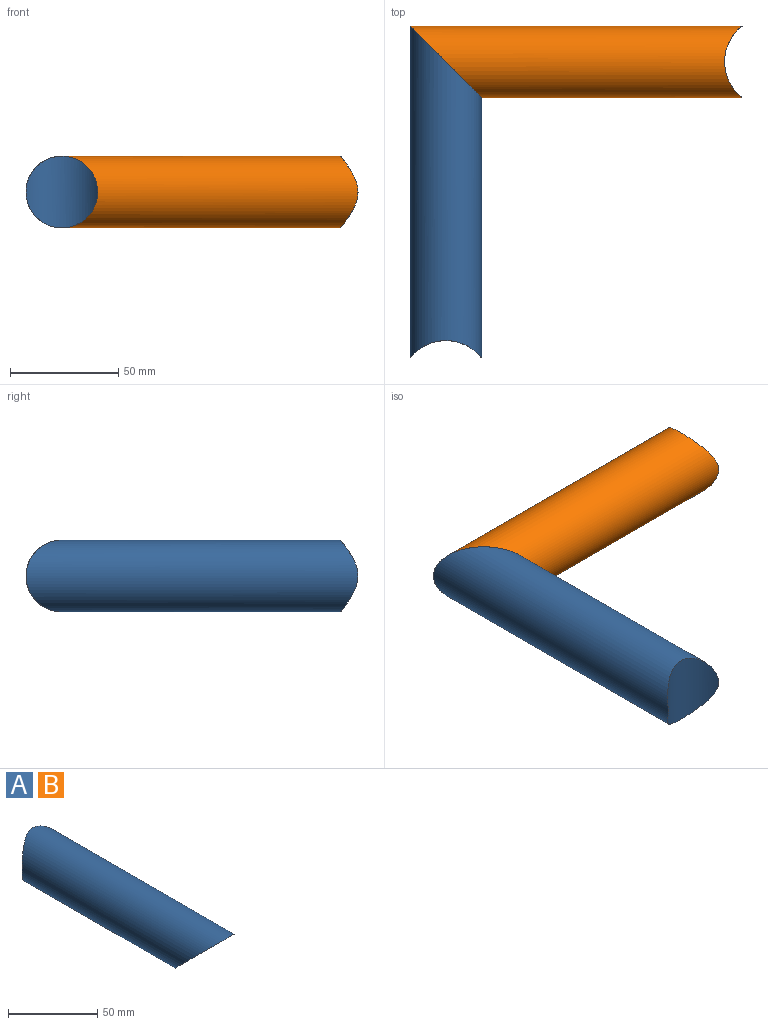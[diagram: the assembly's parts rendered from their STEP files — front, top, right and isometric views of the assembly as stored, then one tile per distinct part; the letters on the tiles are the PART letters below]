
ASSEMBLY  parts=2 mates=1
PART A: 3 faces, bbox 33x153x33 mm
  f0: cylinder r=16.5mm len=153.02mm, axis (0,1,0), area 13712.3mm2, adj f1,f2
  f1: plane 33x33mm, normal (0,-0.71,-0.71), area 1209.6mm2, adj f0
  f2: cylinder r=21mm len=33mm, axis (-1,0,0), area 944.7mm2, adj f0
PART B: same geometry as A
PLACE A rot(axis=(0.71,0,-0.71),180deg) t=(-89.5,-33.63,-102.45)mm
PLACE B rot(axis=(-0.58,-0.58,-0.58),120deg) t=(60,115.87,-102.45)mm
MATE fastened A.f1 <-> B.f1  axis (0.71,0.71,0) through (-89.5,115.87,-102.45)mm
